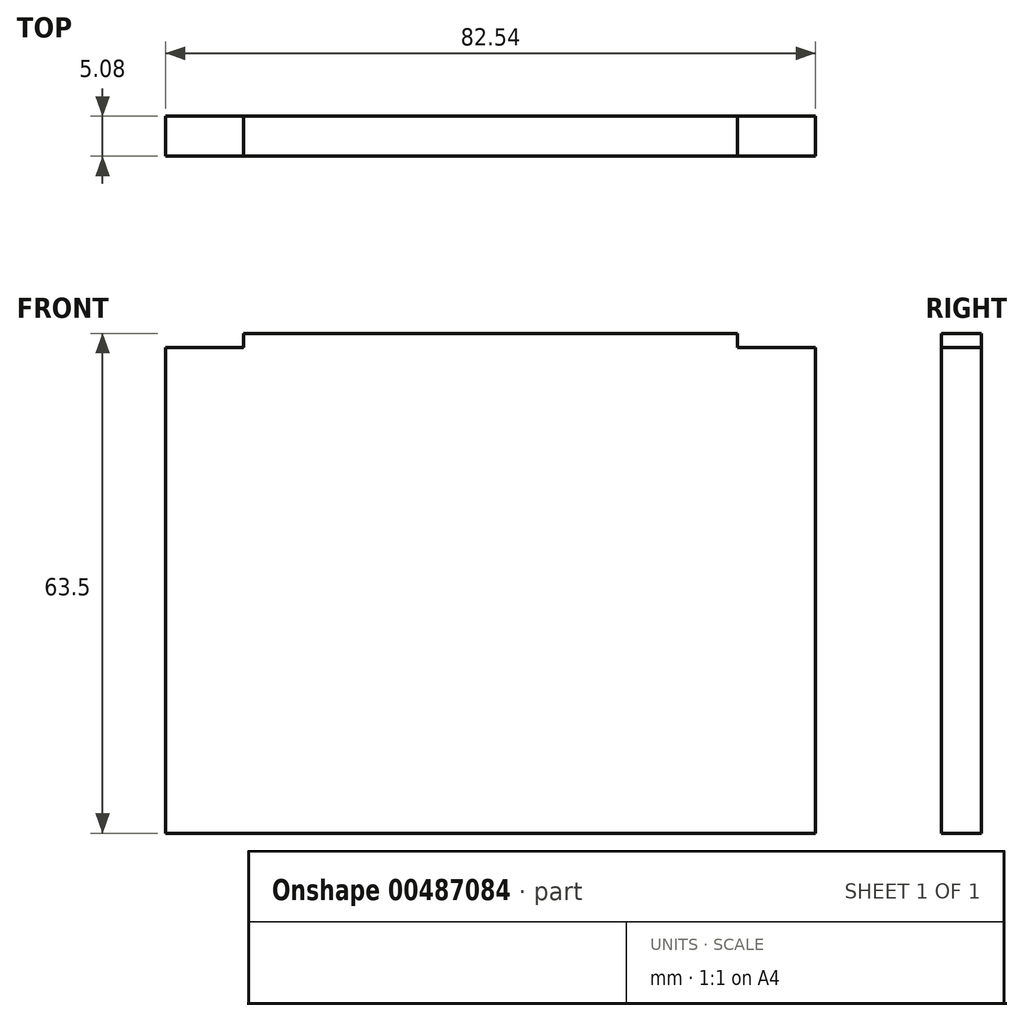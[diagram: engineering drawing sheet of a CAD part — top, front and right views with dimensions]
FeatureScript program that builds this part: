
annotation { "Feature Type Name" : "Feature", "Feature Type Description" : "" }
export const myFeature = defineFeature(function(context is Context, id is Id, definition is map)
    precondition{}
    {
        {
            var Q0;
            Q0=qCreatedBy(makeId("Front.planeOp"),FACE);
            var sketch = newSketch(context, id + "F0", { "sketchPlane" : qUnion([Q0])});
            skLineSegment(sketch, "E0.bottom", {"start": v(-31.37, 0) * mm, "end": v(31.37, 0) * mm});
            skLineSegment(sketch, "E0.top", {"start": v(-41.27, -63.5) * mm, "end": v(41.28, -63.5) * mm});
            skLineSegment(sketch, "E0.left", {"start": v(-41.28, -1.78) * mm, "end": v(-41.27, -63.5) * mm});
            skLineSegment(sketch, "E0.right", {"start": v(41.28, -1.78) * mm, "end": v(41.28, -63.5) * mm});
            skLineSegment(sketch, "E1.top", {"start": v(41.28, -1.78) * mm, "end": v(31.37, -1.78) * mm});
            skLineSegment(sketch, "E1.right", {"start": v(31.37, 0) * mm, "end": v(31.37, -1.78) * mm});
            skLineSegment(sketch, "E2.top", {"start": v(-41.28, -1.78) * mm, "end": v(-31.37, -1.78) * mm});
            skLineSegment(sketch, "E2.right", {"start": v(-31.37, 0) * mm, "end": v(-31.37, -1.78) * mm});
            skSolve(sketch);
        }
        {
            var Q0;
            Q0=makeQuery(id+"F0.imprint","IMPRINT",FACE,{"disambiguationData":[TD([[makeQuery(id+"F0.imprint","IMPRINT",EDGE,{"derivedFrom":sQuery(id+"F0.wireOp",EDGE,"E0.bottom")}),-1.0]])]});
            extrude(context, id + "F1", {"entities" : qUnion([Q0]), "depth" : 5.08 * mm});
        }
    });
